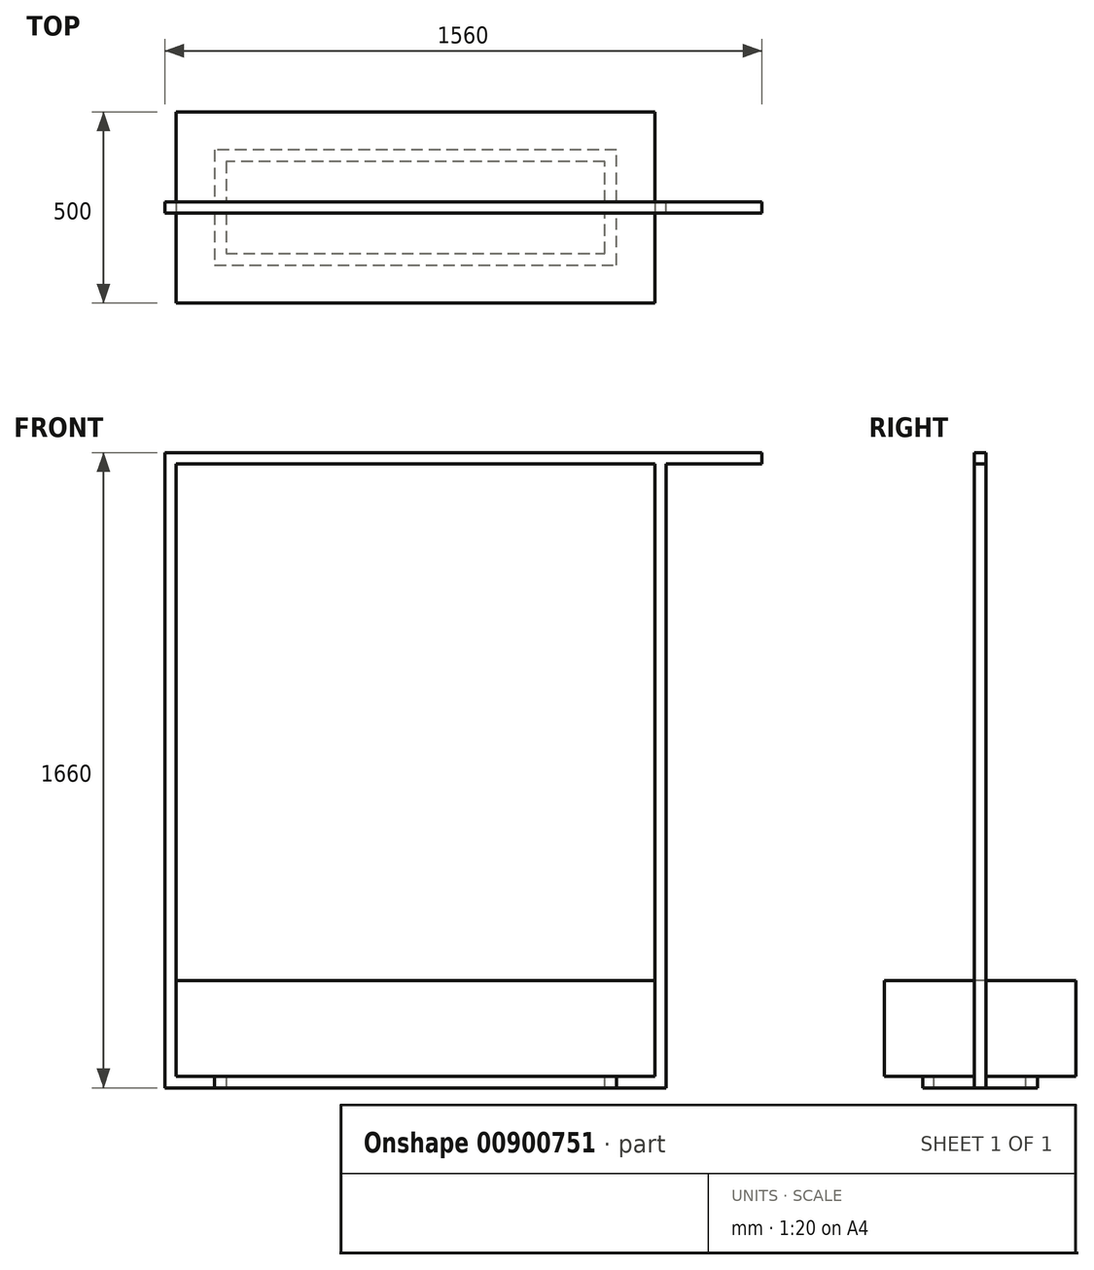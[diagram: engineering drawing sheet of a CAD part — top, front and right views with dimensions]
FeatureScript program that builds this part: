
annotation { "Feature Type Name" : "Feature", "Feature Type Description" : "" }
export const myFeature = defineFeature(function(context is Context, id is Id, definition is map)
    precondition{}
    {
        {
            var Q0;
            Q0=qCreatedBy(makeId("Top.planeOp"),FACE);
            var sketch = newSketch(context, id + "F0", { "sketchPlane" : qUnion([Q0])});
            skLineSegment(sketch, "E0.bottom", {"start": v(-625, 250) * mm, "end": v(625, 250) * mm});
            skLineSegment(sketch, "E0.top", {"start": v(-625, -250) * mm, "end": v(625, -250) * mm});
            skLineSegment(sketch, "E0.left", {"start": v(-625, 250) * mm, "end": v(-625, -250) * mm});
            skLineSegment(sketch, "E0.right", {"start": v(625, 250) * mm, "end": v(625, -250) * mm});
            skLineSegment(sketch, "E1", {"start": v(-625, 250) * mm, "end": v(625, -250) * mm, "construction": true});
            skSolve(sketch);
        }
        {
            var Q0;
            Q0=qSketchRegion(id+"F0",true);
            extrude(context, id + "F1", {"entities" : qUnion([Q0]), "depth" : 250 * mm, "offsetDistance" : 25 * mm});
        }
        {
            var Q0;
            Q0=qCreatedBy(makeId("Front.planeOp"),FACE);
            var sketch = newSketch(context, id + "F2", { "sketchPlane" : qUnion([Q0])});
            skLineSegment(sketch, "E2", {"start": v(625, 0) * mm, "end": v(625, 1600) * mm});
            skLineSegment(sketch, "E3", {"start": v(625, 1600) * mm, "end": v(-625, 1600) * mm});
            skLineSegment(sketch, "E4", {"start": v(-625, 1600) * mm, "end": v(-625, 0) * mm});
            skLineSegment(sketch, "E5", {"start": v(-625, 0) * mm, "end": v(625, 0) * mm});
            skLineSegment(sketch, "E6.0", {"start": v(655, 1630) * mm, "end": v(-655, 1630) * mm});
            skLineSegment(sketch, "E6.1", {"start": v(655, -30) * mm, "end": v(655, 1630) * mm});
            skLineSegment(sketch, "E6.2", {"start": v(-655, -30) * mm, "end": v(655, -30) * mm});
            skLineSegment(sketch, "E6.3", {"start": v(-655, 1630) * mm, "end": v(-655, -30) * mm});
            skSolve(sketch);
        }
        {
            var Q0;
            Q0=qSketchRegion(id+"F2",true);
            extrude(context, id + "F3", {"entities" : qUnion([Q0]), "endBound" : BoundingType.SYMMETRIC, "depth" : 30 * mm, "offsetDistance" : 25 * mm});
        }
        {
            var Q0;
            Q0=makeQuery(id+"F1.opExtrude","CAP_FACE",FACE,{"disambiguationData":[OSD([sQuery(id+"F0.wireOp",EDGE,"E0.bottom"),sQuery(id+"F0.wireOp",EDGE,"E0.top"),sQuery(id+"F0.wireOp",EDGE,"E0.left"),sQuery(id+"F0.wireOp",EDGE,"E0.right")])],"isStart":true});
            var sketch = newSketch(context, id + "F4", { "sketchPlane" : qUnion([Q0])});
            skLineSegment(sketch, "E7", {"start": v(525, 150) * mm, "end": v(525, -150) * mm});
            skLineSegment(sketch, "E8", {"start": v(525, -150) * mm, "end": v(-525, -150) * mm});
            skLineSegment(sketch, "E9", {"start": v(-525, -150) * mm, "end": v(-525, 150) * mm});
            skLineSegment(sketch, "E10", {"start": v(-525, 150) * mm, "end": v(525, 150) * mm});
            skLineSegment(sketch, "E11.0", {"start": v(-495, 120) * mm, "end": v(495, 120) * mm});
            skLineSegment(sketch, "E11.1", {"start": v(-495, -120) * mm, "end": v(-495, 120) * mm});
            skLineSegment(sketch, "E11.2", {"start": v(495, -120) * mm, "end": v(-495, -120) * mm});
            skLineSegment(sketch, "E11.3", {"start": v(495, 120) * mm, "end": v(495, -120) * mm});
            skSolve(sketch);
        }
        {
            var Q0;
            Q0=qSketchRegion(id+"F4",true);
            extrude(context, id + "F5", {"entities" : qUnion([Q0]), "operationType" : NewBodyOperationType.ADD, "depth" : 30 * mm, "offsetDistance" : 25 * mm});
        }
        {
            var Q0;
            Q0=makeQuery(id+"F3.opExtrude","SWEPT_FACE",FACE,{"disambiguationData":[OSD([sQuery(id+"F2.wireOp",EDGE,"E6.1")])]});
            var sketch = newSketch(context, id + "F6", { "sketchPlane" : qUnion([Q0])});
            skLineSegment(sketch, "E12.bottom", {"start": v(-15, 1630) * mm, "end": v(15, 1630) * mm});
            skLineSegment(sketch, "E12.top", {"start": v(-15, 1600) * mm, "end": v(15, 1600) * mm});
            skLineSegment(sketch, "E12.left", {"start": v(-15, 1630) * mm, "end": v(-15, 1600) * mm});
            skLineSegment(sketch, "E12.right", {"start": v(15, 1630) * mm, "end": v(15, 1600) * mm});
            skSolve(sketch);
        }
        {
            var Q0;
            Q0 = qSketchRegion(id + "F6", true);
            extrude(context, id + "F7", {"entities" : qUnion([Q0]), "operationType" : NewBodyOperationType.ADD, "depth" : 250 * mm, "offsetDistance" : 25 * mm});
        }
    });
